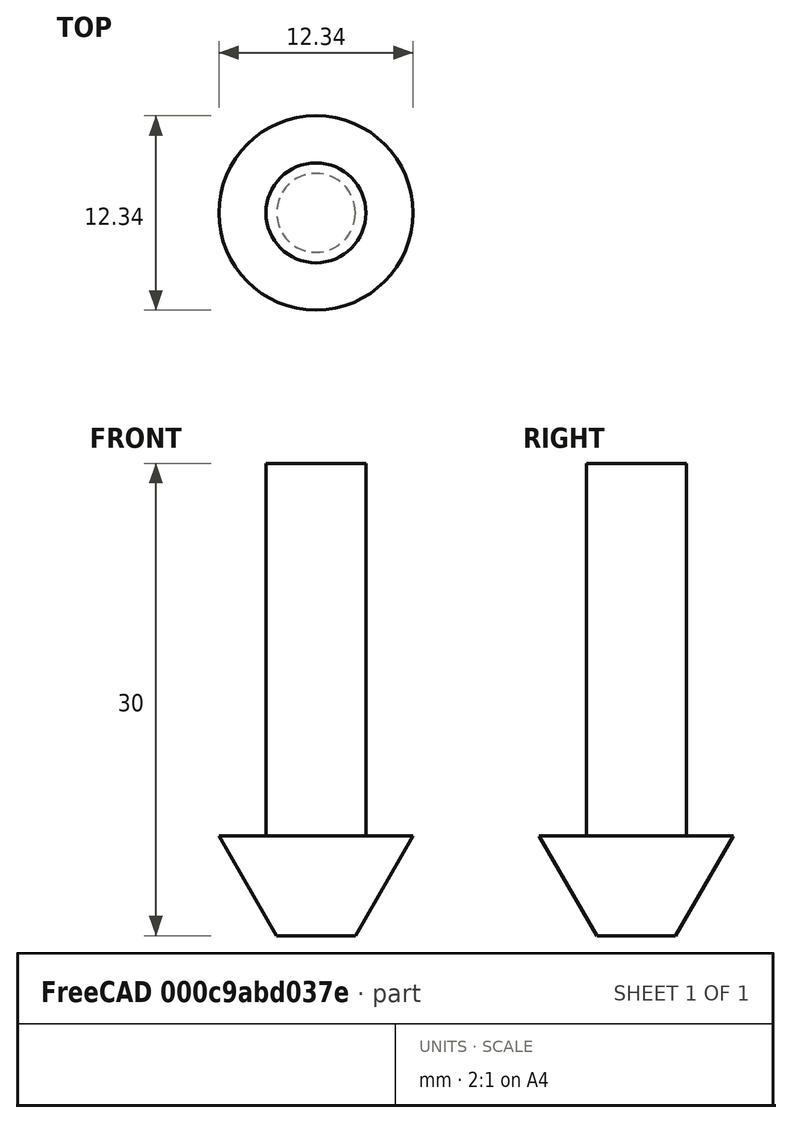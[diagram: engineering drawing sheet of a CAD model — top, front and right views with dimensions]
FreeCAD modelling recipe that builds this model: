
FCSTD DOCUMENT  (FreeCAD 1.0R39109 (Git))
Label: chamfer
License: Creative Commons Attribution 4.0
LicenseURL: https://creativecommons.org/licenses/by/4.0/
objects: Sketcher::SketchObject×1, PartDesign::Revolution×1, App::FeaturePython×1, PartDesign::Body×1
note: 6 computed .brp shape members not serialized (recipe doc carries the construction recipe); baked Part::Feature solids carry a one-line shape summary decoded from their .brp

FEATURE [Sketcher::SketchObject] Sketch
  ArcFitTolerance = 0
  AttachmentSupport = -> [XZ_Plane]
  FullyConstrained = true
  MakeInternals = false
  MapMode = 5
  Placement = pos=(0,0,0) rot=(1,0,0;1.5708rad)
  expr: Constraints[10] = <<Attributes>>.CuttingEdgeHeight
  expr: Constraints[13] = <<Attributes>>.ShankDiameter / 2
  expr: Constraints[14] = <<Attributes>>.TipDiameter / 2 + 1 um
  expr: Constraints[16] = <<Attributes>>.CuttingEdgeAngle / 2
  expr: Constraints[5] = <<Attributes>>.Length
  sketch-geometry (6):
    g0: LineSegment StartX=0 StartY=30 StartZ=0 EndX=0 EndY=0 EndZ=0
    g1: LineSegment StartX=0 StartY=0 StartZ=0 EndX=2.501 EndY=0 EndZ=0
    g2: LineSegment StartX=2.501 StartY=0 StartZ=0 EndX=6.16717 EndY=6.35 EndZ=0
    g3: LineSegment StartX=3.175 StartY=30 StartZ=0 EndX=0 EndY=30 EndZ=0
    g4: LineSegment StartX=3.175 StartY=6.36 StartZ=0 EndX=6.16717 EndY=6.35 EndZ=0
    g5: LineSegment StartX=3.175 StartY=30 StartZ=0 EndX=3.175 EndY=6.36 EndZ=0
  constraints (17):
    c: Vertical(g0)
    c: Coincident(g0,g1)
    c: Horizontal(g1)
    c: Coincident(g1,g2)
    c: Horizontal(g3)
    c: DistanceY(g2,g3) = 30
    c: Coincident(g2,g4)
    c: Vertical(g5)
    c: Coincident(g3,g5)
    c: Coincident(g4,g5)
    c: DistanceY(g2) = 6.35
    c: Coincident(g0,g-1)
    c: Coincident(g0,g3)
    c: DistanceX(g-2,g3) = 3.175
    c: DistanceX(g-2,g1) = 2.501
    c: DistanceY(g2,g4) = 0.01
    c: Angle(g2,g-2) = 0.523599
FEATURE [PartDesign::Revolution] Revolution
  AllowMultiFace = false
  Angle = 360
  Angle2 = 60
  Axis = (0,2e-16,1)
  Base = (0,0,0)
  Placement = pos=(0,0,0) rot=(1,0,0;1.5708rad)
  Profile = -> Sketch
  ReferenceAxis = -> Sketch [V_Axis]
  Reversed = true
  Suppressed = false
  Type = 0
FEATURE [App::FeaturePython] PropertyBag  label="Attributes"  # WARN: FeaturePython — macro-defined, semantics opaque (R4)
  CustomPropertyGroups = 0
  CuttingEdgeAngle = 60
  CuttingEdgeHeight = 6.35
  Diameter = 12
  Flutes = 2
  Length = 30
  ShankDiameter = 6.35
  TipDiameter = 5
FEATURE [PartDesign::Body] Body  label="Chamfer"
  AllowCompound = false
  Group = -> [Sketch,Revolution,PropertyBag]
  Origin = -> Origin
  Tip = -> Revolution
